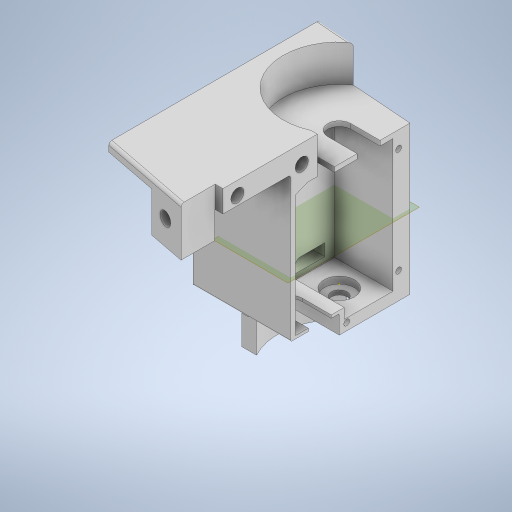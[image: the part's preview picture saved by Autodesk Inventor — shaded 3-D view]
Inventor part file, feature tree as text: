
AUTODESK INVENTOR PART (.ipt)
format: ipt  version: 2023.5 (Build 275446000, 446)  size: 1,212,928 bytes
history: native  units: mm
features: sketch x69, extrude x62, projected_geometry x47, reference x33, other x16, fillet x16, hole x6
ambient origin geometry x8: Origin, YZ Plane, XZ Plane, XY Plane, X Axis, Y Axis, Z Axis, Center Point
bodies: Body1 (feature_tree), Body2 (feature_tree)
feature tree (249):
  other  "Bryła1"
  extrude  "Wyciągnięcie proste1"  Depth=3.2mm
  extrude  "Wyciągnięcie proste2"  Depth=6.0mm
  extrude  "Wyciągnięcie proste3"  Depth=6.0mm
  extrude  "Wyciągnięcie proste4"  Depth=1.0mm TaperAngle=0.0deg
  extrude  "Wyciągnięcie proste5"  Depth=5.7mm
  extrude  "Wyciągnięcie proste6"  Depth=2.0mm TaperAngle=0.0deg
  extrude  "Wyciągnięcie proste7"  Depth=1.0mm TaperAngle=0.0deg
  extrude  "Wyciągnięcie proste8"  Depth=3.5mm
  extrude  "Wyciągnięcie proste9"  Depth=2.0mm TaperAngle=0.0deg
  extrude  "Wyciągnięcie proste10"  Depth=2.0mm TaperAngle=0.0deg
  extrude  "Wyciągnięcie proste11"  Depth=10.0mm TaperAngle=0.0deg
  extrude  "Wyciągnięcie proste12"  Depth=1.0mm
  extrude  "Wyciągnięcie proste13"  Depth=10.0mm TaperAngle=0.0deg
  extrude  "Wyciągnięcie proste14"  Depth=10.0mm TaperAngle=0.0deg
  extrude  "Wyciągnięcie proste15"  Depth=0.5mm
  extrude  "Wyciągnięcie proste16"  Depth=10.0mm TaperAngle=0.0deg
  sketch  "Szkic17"
  hole  "Otwór1"  [1 undecoded]
  other  "Płaszczyzna konstrukcyjna1"
  hole  "Otwór3"  [1 undecoded]
  extrude  "Wyciągnięcie proste18"  Depth=10.0mm TaperAngle=0.0deg
  extrude  "Wyciągnięcie proste19"  Depth=10.0mm TaperAngle=0.0deg
  hole  "Otwór4"  [1 undecoded]
  sketch  "Szkic24"
  other  "Płaszczyzna konstrukcyjna2"
  other  "Płaszczyzna konstrukcyjna3"
  extrude  "Wyciągnięcie proste20"  Depth=0.4mm
  extrude  "Wyciągnięcie proste21"  Depth=0.6mm TaperAngle=0.0deg
  extrude  "Wyciągnięcie proste22"  Depth=0.4mm
  fillet  "Zaokrąglenie1"  Radius=2.0mm
  extrude  "Wyciągnięcie proste23"  Depth=1.0mm TaperAngle=0.0deg
  extrude  "Wyciągnięcie proste24"  Depth=1.0mm TaperAngle=0.0deg
  extrude  "Wyciągnięcie proste25"  Depth=0.5mm
  extrude  "Wyciągnięcie proste26"  Depth=2.75mm
  extrude  "Wyciągnięcie proste27"  Depth=3.0mm
  extrude  "Wyciągnięcie proste28"  Depth=3.0mm
  extrude  "Wyciągnięcie proste29"  Depth=10.0mm TaperAngle=0.0deg
  extrude  "Wyciągnięcie proste30"  Depth=1.0mm
  extrude  "Wyciągnięcie proste31"  Depth=10.0mm
  hole  "Otwór5"  [1 undecoded]
  extrude  "Wyciągnięcie proste32"  Depth=2.75mm
  extrude  "Wyciągnięcie proste33"  Depth=2.75mm
  sketch  "Szkic40"
  sketch  "Szkic41"
  extrude  "Wyciągnięcie proste34"  Depth=10.0mm TaperAngle=0.0deg
  extrude  "Wyciągnięcie proste35"  Depth=10.0mm TaperAngle=0.0deg
  extrude  "Wyciągnięcie proste36"  Depth=4.0mm TaperAngle=0.0deg
  extrude  "Wyciągnięcie proste37"  Depth=5.0mm
  extrude  "Wyciągnięcie proste38"  Depth=4.0mm TaperAngle=0.0deg
  fillet  "Zaokrąglenie3"  Radius=10.0mm
  fillet  "Zaokrąglenie4"  Radius=10.0mm
  extrude  "Wyciągnięcie proste39"  Depth=5.0mm TaperAngle=0.0deg
  extrude  "Wyciągnięcie proste40"  Depth=1.8mm TaperAngle=0.0deg
  fillet  "Zaokrąglenie5"  Radius=1.8mm
  extrude  "Wyciągnięcie proste41"  Depth=10.0mm TaperAngle=0.0deg
  extrude  "Wyciągnięcie proste42"  Depth=10.0mm TaperAngle=0.0deg
  extrude  "Wyciągnięcie proste43"  Depth=1.0mm TaperAngle=0.0deg
  extrude  "Wyciągnięcie proste44"  Depth=3.5mm
  sketch  "Szkic51"
  extrude  "Wyciągnięcie proste45"  Depth=2.3mm
  extrude  "Wyciągnięcie proste46"  Depth=1.0mm TaperAngle=0.0deg
  extrude  "Wyciągnięcie proste47"  TaperAngle=0.0deg  [1 undecoded]
  extrude  "Wyciągnięcie proste48"  Depth=0.5mm
  extrude  "Wyciągnięcie proste49"  Depth=0.5mm
  fillet  "Zaokrąglenie6"  Radius=4.0mm
  extrude  "Wyciągnięcie proste50"  Depth=0.5mm
  extrude  "Wyciągnięcie proste51"  Depth=0.5mm
  fillet  "Zaokrąglenie7"  Radius=0.5mm
  extrude  "Wyciągnięcie proste52"  Depth=0.5mm
  fillet  "Zaokrąglenie8"  Radius=0.5mm
  fillet  "Zaokrąglenie9"  Radius=0.2mm
  extrude  "Wyciągnięcie proste53"  Depth=2.0mm TaperAngle=0.0deg
  extrude  "Wyciągnięcie proste54"  Depth=2.0mm TaperAngle=0.0deg
  fillet  "Zaokrąglenie10"  Radius=10.0mm
  extrude  "Wyciągnięcie proste55"  Depth=10.0mm TaperAngle=0.0deg
  fillet  "Zaokrąglenie12"  Radius=2.0mm
  hole  "Otwór6"  [1 undecoded]
  extrude  "Wyciągnięcie proste56"  TaperAngle=0.0deg  [1 undecoded]
  hole  "Otwór7"  [1 undecoded]
  extrude  "Wyciągnięcie proste57"  Depth=1.0mm
  extrude  "Wyciągnięcie proste58"  Depth=2.0mm TaperAngle=0.0deg
  extrude  "Wyciągnięcie proste59"  Depth=2.0mm TaperAngle=0.0deg
  sketch  "Szkic67"
  extrude  "Wyciągnięcie proste60"  Depth=10.0mm TaperAngle=0.0deg
  extrude  "Wyciągnięcie proste61"  Depth=10.0mm TaperAngle=0.0deg
  extrude  "Wyciągnięcie proste62"  Depth=15.0mm TaperAngle=0.0deg
  fillet  "Zaokrąglenie13"  Radius=10.0mm
  fillet  "Zaokrąglenie14"  Radius=0.5mm
  fillet  "Zaokrąglenie15"  Radius=0.5mm
  fillet  "Zaokrąglenie16"  Radius=10.0mm
  extrude  "Wyciągnięcie proste63"  Depth=2.0mm
  fillet  "Zaokrąglenie17"  Radius=10.0mm
  fillet  "Zaokrąglenie18"  Radius=10.0mm
  sketch  "Szkic1"
  sketch  "Szkic2"
  projected_geometry  "Pętla rzutowana1"
  sketch  "Szkic3"
  projected_geometry  "Pętla rzutowana2"
  sketch  "Szkic4"
  reference  "Odniesienie1"
  reference  "Odniesienie2"
  projected_geometry  "Pętla rzutowana3"
  reference  "Odniesienie3"
  reference  "Odniesienie4"
  reference  "Odniesienie5"
  sketch  "Szkic5"
  reference  "Odniesienie6"
  reference  "Odniesienie7"
  sketch  "Szkic6"
  reference  "Odniesienie8"
  sketch  "Szkic7"
  projected_geometry  "Pętla rzutowana4"
  sketch  "Szkic8"
  sketch  "Szkic9"
  reference  "Odniesienie9"
  sketch  "Szkic10"
  reference  "Odniesienie10"
  projected_geometry  "Pętla rzutowana5"
  sketch  "Szkic11"
  reference  "Odniesienie11"
  projected_geometry  "Pętla rzutowana6"
  sketch  "Szkic12"
  sketch  "Szkic13"
  projected_geometry  "Pętla rzutowana7"
  sketch  "Szkic14"
  reference  "Odniesienie12"
  reference  "Odniesienie13"
  sketch  "Szkic15"
  reference  "Odniesienie14"
  reference  "Odniesienie15"
  reference  "Odniesienie16"
  sketch  "Szkic16"
  projected_geometry  "Pętla rzutowana8"
  reference  "Odniesienie17"
  reference  "Odniesienie18"
  sketch  "Szkic18"
  projected_geometry  "Pętla rzutowana9"
  sketch  "Szkic20"
  projected_geometry  "Pętla rzutowana10"
  sketch  "Szkic21"
  reference  "Odniesienie19"
  reference  "Odniesienie20"
  reference  "Odniesienie21"
  reference  "Odniesienie22"
  sketch  "Szkic22"
  reference  "Odniesienie23"
  reference  "Odniesienie24"
  sketch  "Szkic23"
  projected_geometry  "Pętla rzutowana11"
  reference  "Odniesienie25"
  sketch  "Szkic26"
  projected_geometry  "Pętla rzutowana12"
  sketch  "Szkic27"
  reference  "Odniesienie26"
  reference  "Odniesienie27"
  sketch  "Szkic28"
  projected_geometry  "Pętla rzutowana13"
  sketch  "Szkic29"
  projected_geometry  "Pętla rzutowana14"
  sketch  "Szkic30"
  sketch  "Szkic31"
  projected_geometry  "Pętla rzutowana15"
  reference  "Odniesienie28"
  reference  "Odniesienie29"
  sketch  "Szkic32"
  reference  "Odniesienie30"
  reference  "Odniesienie31"
  sketch  "Szkic33"
  projected_geometry  "Pętla rzutowana16"
  sketch  "Szkic34"
  projected_geometry  "Pętla rzutowana17"
  sketch  "Szkic35"
  projected_geometry  "Pętla rzutowana18"
  sketch  "Szkic36"
  projected_geometry  "Pętla rzutowana19"
  sketch  "Szkic37"
  projected_geometry  "Pętla rzutowana20"
  sketch  "Szkic38"
  sketch  "Szkic39"
  projected_geometry  "Pętla rzutowana21"
  reference  "Odniesienie32"
  reference  "Odniesienie33"
  sketch  "Szkic42"
  projected_geometry  "Pętla rzutowana22"
  sketch  "Szkic43"
  projected_geometry  "Pętla rzutowana23"
  projected_geometry  "Pętla rzutowana24"
  sketch  "Szkic44"
  projected_geometry  "Pętla rzutowana25"
  projected_geometry  "Pętla rzutowana26"
  sketch  "Szkic45"
  projected_geometry  "Pętla rzutowana27"
  sketch  "Szkic46"
  projected_geometry  "Pętla rzutowana28"
  sketch  "Szkic47"
  sketch  "Szkic48"
  sketch  "Szkic49"
  projected_geometry  "Pętla rzutowana29"
  sketch  "Szkic50"
  projected_geometry  "Pętla rzutowana30"
  projected_geometry  "Pętla rzutowana31"
  projected_geometry  "Pętla rzutowana32"
  sketch  "Szkic52"
  sketch  "Szkic53"
  projected_geometry  "Pętla rzutowana33"
  sketch  "Szkic54"
  projected_geometry  "Pętla rzutowana34"
  sketch  "Szkic55"
  projected_geometry  "Pętla rzutowana35"
  sketch  "Szkic56"
  sketch  "Szkic57"
  projected_geometry  "Pętla rzutowana36"
  sketch  "Szkic58"
  projected_geometry  "Pętla rzutowana37"
  sketch  "Szkic59"
  projected_geometry  "Pętla rzutowana38"
  projected_geometry  "Pętla rzutowana39"
  sketch  "Szkic60"
  projected_geometry  "Pętla rzutowana40"
  sketch  "Szkic61"
  projected_geometry  "Pętla rzutowana41"
  sketch  "Szkic62"
  projected_geometry  "Pętla rzutowana42"
  sketch  "Szkic63"
  projected_geometry  "Pętla rzutowana43"
  sketch  "Szkic64"
  sketch  "Szkic65"
  sketch  "Szkic66"
  projected_geometry  "Pętla rzutowana44"
  sketch  "Szkic68"
  projected_geometry  "Pętla rzutowana45"
  sketch  "Szkic69"
  projected_geometry  "Pętla rzutowana46"
  sketch  "Szkic70"
  projected_geometry  "Pętla rzutowana47"
  sketch  "Szkic71"
  parser-record x1  (decoder bookkeeping rows leaked as tree rows — omitted from the tree; the rows remain in map.json)
  other  "stratos_v2_mechanics.iam"
  other  "silnik:2"
  other  "silnik:1"
  other  "lipo-300:1"
  other  "podstawa_v2:1"
  other  "kolo:1"
  other  "kolo:2"
  other  "wymiar:1"
  other  "MikroSumo:1"
  other  "nozzyk:1"
  other  "scianka_prawa:1"
note: 8 required parameter values undecoded (feature->parameter linkage not recoverable at this tier; creation-order binding heuristic only, values carry confidence <= 0.55)
note: 1 file-system path scrubbed to <path> (originals preserved in map.json)
